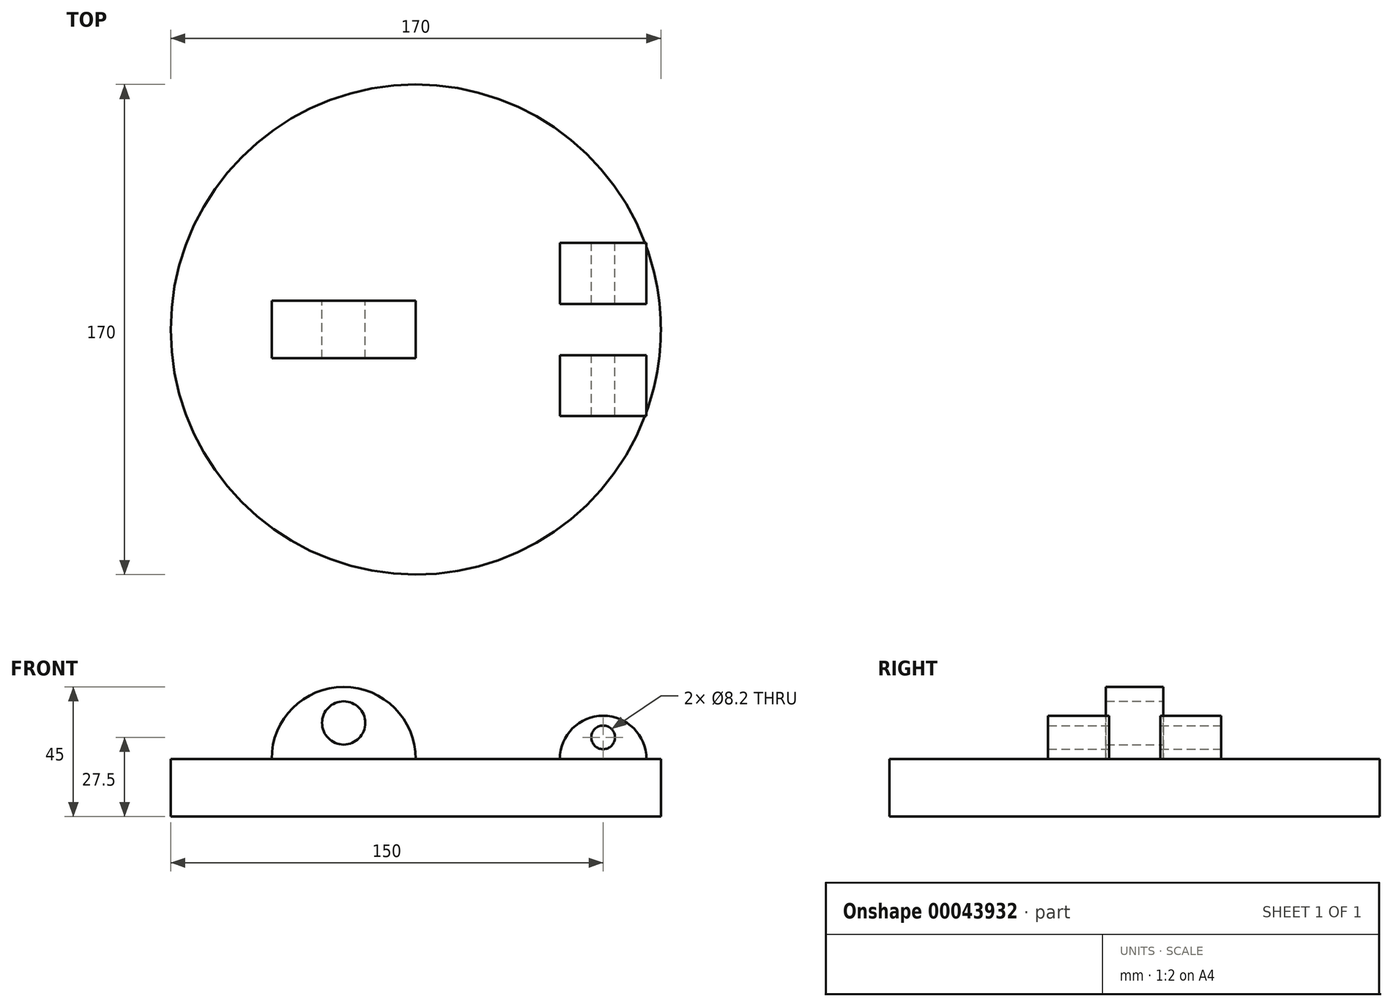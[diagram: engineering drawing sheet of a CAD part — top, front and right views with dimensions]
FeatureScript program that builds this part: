
annotation { "Feature Type Name" : "Feature", "Feature Type Description" : "" }
export const myFeature = defineFeature(function(context is Context, id is Id, definition is map)
    precondition{}
    {
        {
            var Q0;
            Q0=qCreatedBy(makeId("Top.planeOp"),FACE);
            var sketch = newSketch(context, id + "F0", { "sketchPlane" : qUnion([Q0])});
            skCircle(sketch, "E0", {"center": v(0, 0) * mm, "radius": 85 * mm});
            skSolve(sketch);
        }
        {
            var Q0;
            Q0 = qSketchRegion(id + "F0", true);
            extrude(context, id + "F1", {"entities" : qUnion([Q0]), "oppositeDirection" : true, "depth" : 20 * mm});
        }
        {
            var Q0;
            Q0=qCreatedBy(makeId("Front.planeOp"),FACE);
            var sketch = newSketch(context, id + "F2", { "sketchPlane" : qUnion([Q0])});
            skLineSegment(sketch, "E1", {"start": v(0, 0) * mm, "end": v(-25, 0) * mm, "construction": true});
            skArc(sketch, "E2", {"start": v(0, 0) * mm, "mid": v(-25, 25) * mm, "end": v(-50, 0) * mm});
            skLineSegment(sketch, "E3", {"start": v(-25, 0) * mm, "end": v(-25, 12.5) * mm});
            skCircle(sketch, "E4", {"center": v(-25, 12.5) * mm, "radius": 7.5 * mm});
            skLineSegment(sketch, "E5", {"start": v(-50, 0) * mm, "end": v(0, 0) * mm});
            skSolve(sketch);
        }
        {
            var Q0;
            Q0 = qSketchRegion(id + "F2", true);
            extrude(context, id + "F3", {"entities" : qUnion([Q0]), "operationType" : NewBodyOperationType.ADD, "depth" : 10 * mm, "hasSecondDirection" : true, "secondDirectionOppositeDirection" : true, "secondDirectionDepth" : 10 * mm});
        }
        {
            var Q0;
            Q0=qCreatedBy(makeId("Front.planeOp"),FACE);
            var sketch = newSketch(context, id + "F4", { "sketchPlane" : qUnion([Q0])});
            skLineSegment(sketch, "E6", {"start": v(50, 0) * mm, "end": v(80, 0) * mm});
            skLineSegment(sketch, "E7", {"start": v(0, 0) * mm, "end": v(65, 0) * mm, "construction": true});
            skArc(sketch, "E8", {"start": v(80, 0) * mm, "mid": v(65, 15) * mm, "end": v(50, 0) * mm});
            skCircle(sketch, "E9", {"center": v(65, 7.5) * mm, "radius": 4.1 * mm});
            skLineSegment(sketch, "E10", {"start": v(65, 0) * mm, "end": v(65, 7.5) * mm});
            skSolve(sketch);
        }
        {
            var Q0;
            Q0 = qSketchRegion(id + "F4", true);
            extrude(context, id + "F5", {"entities" : qUnion([Q0]), "operationType" : NewBodyOperationType.ADD, "depth" : 30 * mm, "hasSecondDirection" : true, "secondDirectionOppositeDirection" : true, "secondDirectionDepth" : 30 * mm});
        }
        {
            var Q0;
            Q0=qCreatedBy(makeId("Top.planeOp"),FACE);
            var sketch = newSketch(context, id + "F6", { "sketchPlane" : qUnion([Q0])});
            skLineSegment(sketch, "E11", {"start": v(0, 0) * mm, "end": v(0, 10) * mm});
            skLineSegment(sketch, "E12", {"start": v(0, 0) * mm, "end": v(0, -10) * mm});
            skLineSegment(sketch, "E13.bottom", {"start": v(0, 8.88) * mm, "end": v(150, 8.88) * mm});
            skLineSegment(sketch, "E13.top", {"start": v(0, -8.88) * mm, "end": v(150, -8.88) * mm});
            skLineSegment(sketch, "E13.left", {"start": v(0, 8.88) * mm, "end": v(0, -8.88) * mm});
            skLineSegment(sketch, "E13.right", {"start": v(150, 8.88) * mm, "end": v(150, -8.88) * mm});
            skSolve(sketch);
        }
        {
            var Q0;
            Q0 = qSketchRegion(id + "F6", true);
            extrude(context, id + "F7", {"entities" : qUnion([Q0]), "operationType" : NewBodyOperationType.REMOVE, "depth" : 25 * mm});
        }
    });
